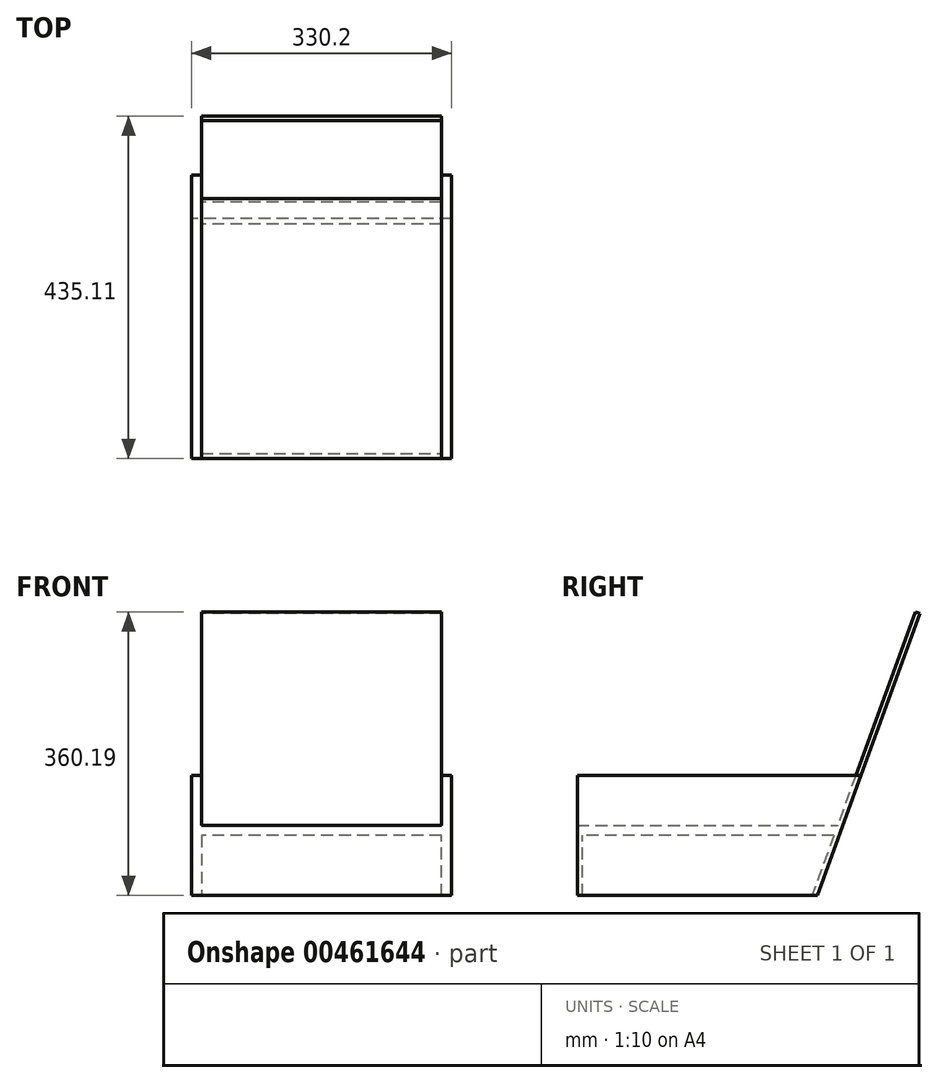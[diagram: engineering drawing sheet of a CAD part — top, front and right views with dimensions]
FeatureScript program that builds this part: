
annotation { "Feature Type Name" : "Feature", "Feature Type Description" : "" }
export const myFeature = defineFeature(function(context is Context, id is Id, definition is map)
    precondition{}
    {
        {
            var Q0;
            Q0=qCreatedBy(makeId("Right.planeOp"),FACE);
            var sketch = newSketch(context, id + "F0", { "sketchPlane" : qUnion([Q0])});
            skLineSegment(sketch, "E0", {"start": v(0, 0) * mm, "end": v(304.8, 0) * mm});
            skLineSegment(sketch, "E1", {"start": v(304.8, 0) * mm, "end": v(360.27, 152.4) * mm});
            skLineSegment(sketch, "E2", {"start": v(360.27, 152.4) * mm, "end": v(0, 152.4) * mm});
            skLineSegment(sketch, "E3", {"start": v(0, 152.4) * mm, "end": v(0, 0) * mm});
            skSolve(sketch);
        }
        {
            var Q0;
            Q0=makeQuery(id+"F0.imprint","IMPRINT",FACE,{"disambiguationData":[TD([[makeQuery(id+"F0.imprint","IMPRINT",EDGE,{"derivedFrom":sQuery(id+"F0.wireOp",EDGE,"E0")}),1.0]])]});
            extrude(context, id + "F1", {"entities" : qUnion([Q0]), "depth" : 12.7 * mm});
        }
        {
            var Q0;
            Q0=makeQuery(id+"F1.opExtrude","CAP_FACE",FACE,{"disambiguationData":[OSD([sQuery(id+"F0.wireOp",EDGE,"E0"),sQuery(id+"F0.wireOp",EDGE,"E1"),sQuery(id+"F0.wireOp",EDGE,"E2"),sQuery(id+"F0.wireOp",EDGE,"E3")])],"isStart":false});
            var sketch = newSketch(context, id + "F2", { "sketchPlane" : qUnion([Q0])});
            skLineSegment(sketch, "E4", {"start": v(298.04, 0) * mm, "end": v(304.8, 0) * mm});
            skLineSegment(sketch, "E5", {"start": v(304.8, 0) * mm, "end": v(435.1, 358.02) * mm});
            skLineSegment(sketch, "E6", {"start": v(435.1, 358.02) * mm, "end": v(429.14, 360.2) * mm});
            skLineSegment(sketch, "E7", {"start": v(429.14, 360.2) * mm, "end": v(298.04, 0) * mm});
            skSolve(sketch);
        }
        {
            var Q0;
            {var subQ3=sQuery(id+"F2.wireOp",EDGE,"E6");Q0=makeQuery(id+"F2.imprint","IMPRINT",FACE,{"disambiguationData":[TD([[makeQuery(id+"F2.imprint","IMPRINT",EDGE,{"derivedFrom":subQ3}),1.0]])]});}
            var Q1;
            {var subQ0=sQuery(id+"F2.wireOp",EDGE,"E4");Q1=makeQuery(id+"F2.imprint","IMPRINT",FACE,{"disambiguationData":[TD([[makeQuery(id+"F2.imprint","IMPRINT",EDGE,{"derivedFrom":subQ0}),1.0]])]});}
            extrude(context, id + "F3", {"entities" : qUnion([Q0, Q1]), "operationType" : NewBodyOperationType.ADD, "depth" : 152.4 * mm});
        }
        {
            var Q0;
            Q0=makeQuery(id+"F1.opExtrude","SWEPT_BODY",BODY,{"disambiguationData":[OSD([sQuery(id+"F0.wireOp",EDGE,"E0"),sQuery(id+"F0.wireOp",EDGE,"E1"),sQuery(id+"F0.wireOp",EDGE,"E2"),sQuery(id+"F0.wireOp",EDGE,"E3")])]});
            var Q1;
            Q1=makeQuery(id+"F3.opExtrude","CAP_FACE",FACE,{"disambiguationData":[OSD([sQuery(id+"F2.wireOp",EDGE,"E4"),sQuery(id+"F2.wireOp",EDGE,"E5"),sQuery(id+"F2.wireOp",EDGE,"E6"),sQuery(id+"F2.wireOp",EDGE,"E7")])],"isStart":false});
            mirror(context, id + "F4", {"operationType" : NewBodyOperationType.ADD, "entities" : qUnion([Q0]), "mirrorPlane" : qUnion([Q1])});
        }
        {
            var Q0;
            Q0=qCreatedBy(makeId("Front.planeOp"),FACE);
            var sketch = newSketch(context, id + "F5", { "sketchPlane" : qUnion([Q0])});
            skLineSegment(sketch, "E8.bottom", {"start": v(0, 76.2) * mm, "end": v(317.5, 76.2) * mm});
            skLineSegment(sketch, "E8.top", {"start": v(0, 88.9) * mm, "end": v(317.5, 88.9) * mm});
            skLineSegment(sketch, "E8.left", {"start": v(0, 76.2) * mm, "end": v(0, 88.9) * mm});
            skLineSegment(sketch, "E8.right", {"start": v(317.5, 76.2) * mm, "end": v(317.5, 88.9) * mm});
            skSolve(sketch);
        }
        {
            var Q0;
            Q0 = qSketchRegion(id + "F5", true);
            extrude(context, id + "F6", {"entities" : qUnion([Q0]), "operationType" : NewBodyOperationType.ADD, "oppositeDirection" : true, "depth" : 330.2 * mm});
        }
        {
            var Q0;
            Q0=makeQuery(id+"F6.opExtrude","SWEPT_FACE",FACE,{"disambiguationData":[OSD([sQuery(id+"F5.wireOp",EDGE,"E8.bottom")])]});
            var sketch = newSketch(context, id + "F7", { "sketchPlane" : qUnion([Q0])});
            skLineSegment(sketch, "E9.bottom", {"start": v(12.7, 0) * mm, "end": v(-307.34, 0) * mm});
            skLineSegment(sketch, "E9.top", {"start": v(12.7, -70.12) * mm, "end": v(-307.34, -70.12) * mm});
            skLineSegment(sketch, "E9.left", {"start": v(12.7, 0) * mm, "end": v(12.7, -70.12) * mm});
            skLineSegment(sketch, "E9.right", {"start": v(-307.34, 0) * mm, "end": v(-307.34, -70.12) * mm});
            skSolve(sketch);
        }
        {
            var Q0;
            {var subQ1=makeQuery(id+"F6.opExtrude","SWEPT_FACE",FACE,{"disambiguationData":[OSD([sQuery(id+"F5.wireOp",EDGE,"E8.bottom")])]});var subQ7=makeQuery(id+"F3.opExtrude","SWEPT_FACE",FACE,{"disambiguationData":[OSD([sQuery(id+"F2.wireOp",EDGE,"E7")])]});var subQ8=makeQuery(id+"F6.boolean.opBoolean","INTERSECT",EDGE,{"derivedFrom":[makeQuery(id+"F4.boolean.opBoolean","MERGE",FACE,{"derivedFrom":[subQ7,makeQuery(id+"F4.opPattern","COPY",FACE,{"derivedFrom":subQ7,"instanceName":"1"})]}),subQ1]});Q0=makeQuery(id+"F7.imprint","IMPRINT",FACE,{"disambiguationData":[TD([[makeQuery(id+"F7.imprint","IMPRINT",EDGE,{"derivedFrom":subQ8}),-1.0]])]});}
            var sketch = newSketch(context, id + "F8", { "sketchPlane" : qUnion([Q0])});
            skLineSegment(sketch, "E10.bottom", {"start": v(0, 0) * mm, "end": v(317.5, 0) * mm});
            skLineSegment(sketch, "E10.top", {"start": v(0, -6.35) * mm, "end": v(317.5, -6.35) * mm});
            skLineSegment(sketch, "E10.left", {"start": v(0, 0) * mm, "end": v(0, -6.35) * mm});
            skLineSegment(sketch, "E10.right", {"start": v(317.5, 0) * mm, "end": v(317.5, -6.35) * mm});
            skSolve(sketch);
        }
        {
            var Q0;
            Q0=makeQuery(id+"F8.imprint","IMPRINT",FACE,{"disambiguationData":[TD([[makeQuery(id+"F8.imprint","IMPRINT",EDGE,{"derivedFrom":sQuery(id+"F8.wireOp",EDGE,"E10.bottom")}),-1.0]])]});
            extrude(context, id + "F9", {"entities" : qUnion([Q0]), "operationType" : NewBodyOperationType.ADD, "depth" : 76.2 * mm});
        }
    });
